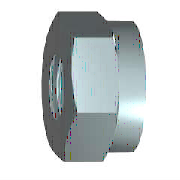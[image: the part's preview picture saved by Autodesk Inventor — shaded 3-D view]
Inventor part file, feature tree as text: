
AUTODESK INVENTOR PART (.ipt)
format: ipt  version: 2024 (Build 280153000, 153)  size: 177,152 bytes
history: native  units: mm (DEFAULTED — no unit token found)
features: extrude x1, chamfer x1, hole x1, other x1, plane x1
ambient origin geometry x7: Origin, YZ Plane, XZ Plane, X Axis, Y Axis, Z Axis, Center Point
bodies: Solid1 (feature_tree), Body (feature_tree)
feature tree (5):
  extrude  "Ring"  Depth=6.350853mm
  chamfer  "Chamfer1"  Distance=2.4mm
  hole  "Thread"  [1 undecoded]
  other  "Work Axis1"
  plane  "Work Plane1"
note: 1 required parameter value undecoded (feature->parameter linkage not recoverable at this tier; creation-order binding heuristic only, values carry confidence <= 0.55)
